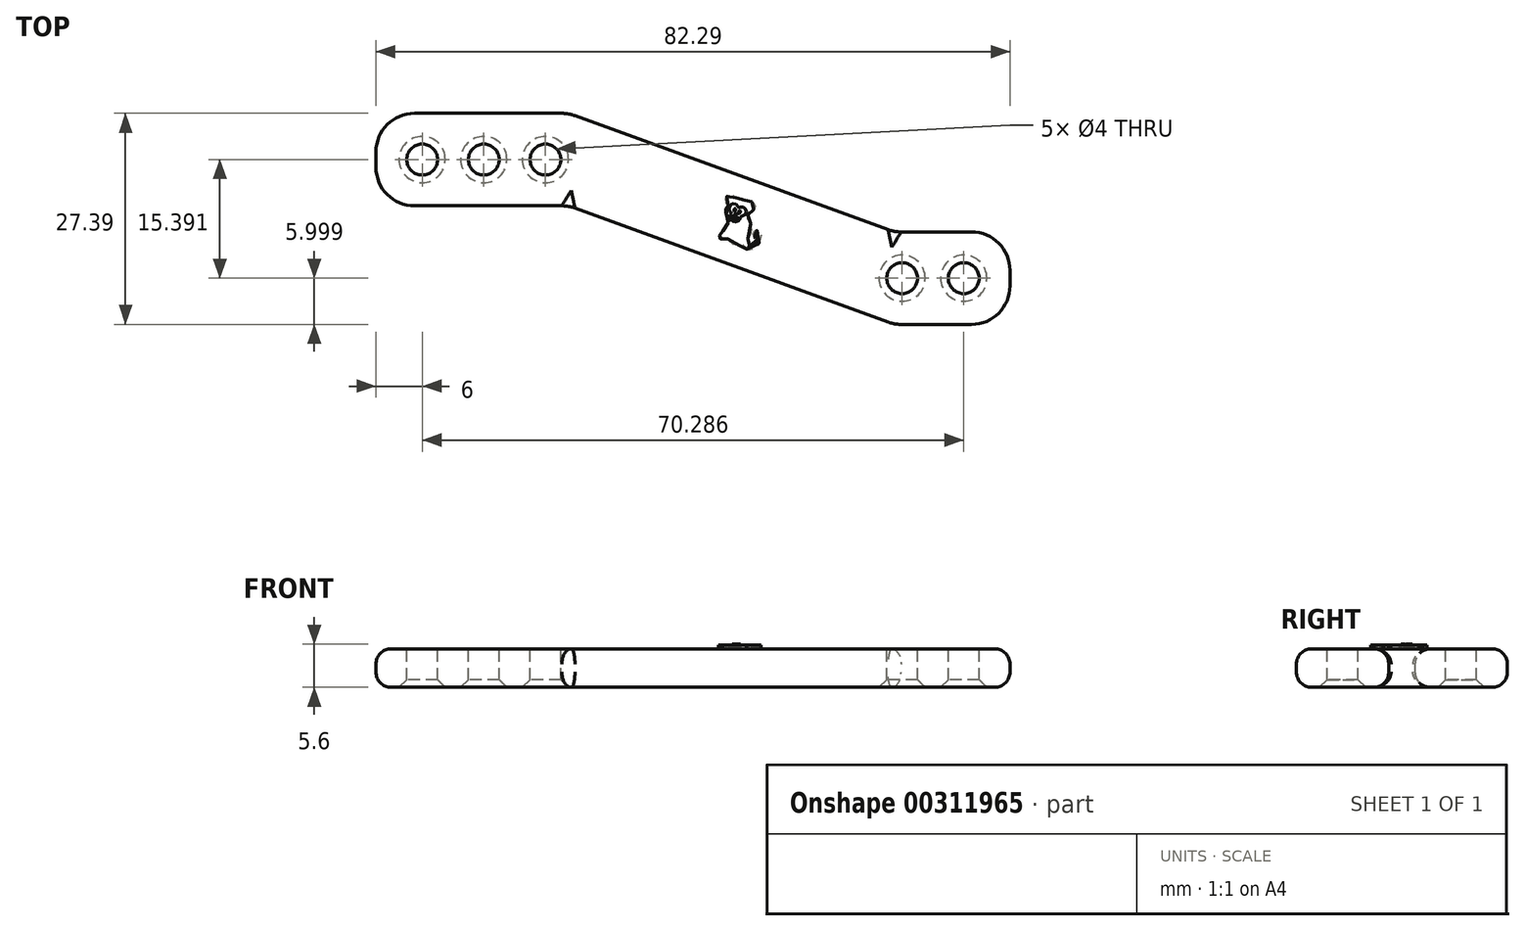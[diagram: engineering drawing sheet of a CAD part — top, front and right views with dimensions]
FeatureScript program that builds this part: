
annotation { "Feature Type Name" : "Feature", "Feature Type Description" : "" }
export const myFeature = defineFeature(function(context is Context, id is Id, definition is map)
    precondition{}
    {
        {
            var Q0;
            Q0=qCreatedBy(makeId("Top.planeOp"),FACE);
            var sketch = newSketch(context, id + "F0", { "sketchPlane" : qUnion([Q0])});
            skLineSegment(sketch, "E0.bottom", {"start": v(0, 12) * mm, "end": v(25, 12) * mm});
            skLineSegment(sketch, "E0.top", {"start": v(0, 0) * mm, "end": v(25, 0) * mm});
            skLineSegment(sketch, "E0.left", {"start": v(0, 12) * mm, "end": v(0, 0) * mm});
            skLineSegment(sketch, "E0.right", {"start": v(25, 12) * mm, "end": v(25, 0) * mm});
            skLineSegment(sketch, "E1.bottom", {"start": v(67.29, -3.4) * mm, "end": v(82.29, -3.4) * mm});
            skLineSegment(sketch, "E1.top", {"start": v(67.29, -15.4) * mm, "end": v(82.29, -15.4) * mm});
            skLineSegment(sketch, "E1.left", {"start": v(67.29, -3.4) * mm, "end": v(67.29, -15.4) * mm});
            skLineSegment(sketch, "E1.right", {"start": v(82.29, -3.4) * mm, "end": v(82.29, -15.4) * mm});
            skLineSegment(sketch, "E2", {"start": v(25, 12) * mm, "end": v(67.29, -3.4) * mm});
            skLineSegment(sketch, "E3", {"start": v(25, 0) * mm, "end": v(67.29, -15.4) * mm});
            skSolve(sketch);
        }
        {
            var Q0;
            Q0=makeQuery(id+"F0.imprint","IMPRINT",FACE,{"disambiguationData":[TD([[makeQuery(id+"F0.imprint","IMPRINT",EDGE,{"derivedFrom":sQuery(id+"F0.wireOp",EDGE,"E1.bottom")}),-1.0]])]});
            var Q1;
            Q1=makeQuery(id+"F0.imprint","IMPRINT",FACE,{"disambiguationData":[TD([[makeQuery(id+"F0.imprint","IMPRINT",EDGE,{"derivedFrom":sQuery(id+"F0.wireOp",EDGE,"E0.right")}),1.0]])]});
            var Q2;
            Q2=makeQuery(id+"F0.imprint","IMPRINT",FACE,{"disambiguationData":[TD([[makeQuery(id+"F0.imprint","IMPRINT",EDGE,{"derivedFrom":sQuery(id+"F0.wireOp",EDGE,"E0.bottom")}),-1.0]])]});
            extrude(context, id + "F1", {"entities" : qUnion([Q0, Q1, Q2]), "depth" : 5 * mm});
        }
        {
            var Q0;
            Q0=makeQuery(id+"F1.opExtrude","CAP_FACE",FACE,{"disambiguationData":[OSD([sQuery(id+"F0.wireOp",EDGE,"E0.bottom"),sQuery(id+"F0.wireOp",EDGE,"E0.top"),sQuery(id+"F0.wireOp",EDGE,"E0.left"),sQuery(id+"F0.wireOp",EDGE,"E1.bottom"),sQuery(id+"F0.wireOp",EDGE,"E1.top"),sQuery(id+"F0.wireOp",EDGE,"E1.right"),sQuery(id+"F0.wireOp",EDGE,"E2"),sQuery(id+"F0.wireOp",EDGE,"E3")])],"isStart":false});
            var sketch = newSketch(context, id + "F2", { "sketchPlane" : qUnion([Q0])});
            skCircle(sketch, "E4", {"center": v(6, 6) * mm, "radius": 2 * mm});
            skCircle(sketch, "E5", {"center": v(76.29, -9.4) * mm, "radius": 2 * mm});
            skCircle(sketch, "E6.1.0.0", {"center": v(14, 6) * mm, "radius": 2 * mm});
            skCircle(sketch, "E6.2.0.0", {"center": v(22, 6) * mm, "radius": 2 * mm});
            skLineSegment(sketch, "E6.direction1", {"start": v(6, 6) * mm, "end": v(14, 6) * mm, "construction": true});
            skCircle(sketch, "E7.1.0.0", {"center": v(68.29, -9.4) * mm, "radius": 2 * mm});
            skLineSegment(sketch, "E7.direction1", {"start": v(76.29, -9.4) * mm, "end": v(68.29, -9.4) * mm, "construction": true});
            skSolve(sketch);
        }
        {
            var Q0;
            Q0 = qSketchRegion(id + "F2", true);
            extrude(context, id + "F3", {"entities" : qUnion([Q0]), "operationType" : NewBodyOperationType.REMOVE, "endBound" : BoundingType.THROUGH_ALL, "oppositeDirection" : true, "depth" : 5 * mm});
        }
        {
            var Q0;
            Q0=makeQuery(id+"F1.opExtrude","CAP_EDGE",EDGE,{"disambiguationData":[OSD([sQuery(id+"F0.wireOp",EDGE,"E0.top")])],"isStart":false});
            var Q1;
            Q1=makeQuery(id+"F1.opExtrude","CAP_EDGE",EDGE,{"disambiguationData":[OSD([sQuery(id+"F0.wireOp",EDGE,"E3")])],"isStart":false});
            var Q2;
            Q2=makeQuery(id+"F1.opExtrude","CAP_EDGE",EDGE,{"disambiguationData":[OSD([sQuery(id+"F0.wireOp",EDGE,"E1.top")])],"isStart":false});
            var Q3;
            Q3=makeQuery(id+"F1.opExtrude","CAP_EDGE",EDGE,{"disambiguationData":[OSD([sQuery(id+"F0.wireOp",EDGE,"E1.right")])],"isStart":false});
            var Q4;
            Q4=makeQuery(id+"F1.opExtrude","CAP_EDGE",EDGE,{"disambiguationData":[OSD([sQuery(id+"F0.wireOp",EDGE,"E1.bottom")])],"isStart":false});
            var Q5;
            Q5=makeQuery(id+"F1.opExtrude","CAP_EDGE",EDGE,{"disambiguationData":[OSD([sQuery(id+"F0.wireOp",EDGE,"E2")])],"isStart":false});
            var Q6;
            Q6=makeQuery(id+"F1.opExtrude","CAP_EDGE",EDGE,{"disambiguationData":[OSD([sQuery(id+"F0.wireOp",EDGE,"E0.bottom")])],"isStart":false});
            var Q7;
            Q7=makeQuery(id+"F1.opExtrude","CAP_EDGE",EDGE,{"disambiguationData":[OSD([sQuery(id+"F0.wireOp",EDGE,"E0.left")])],"isStart":false});
            var Q8;
            Q8=makeQuery(id+"F1.opExtrude","CAP_EDGE",EDGE,{"disambiguationData":[OSD([sQuery(id+"F0.wireOp",EDGE,"E0.bottom")])],"isStart":true});
            var Q9;
            Q9=makeQuery(id+"F1.opExtrude","CAP_EDGE",EDGE,{"disambiguationData":[OSD([sQuery(id+"F0.wireOp",EDGE,"E2")])],"isStart":true});
            var Q10;
            Q10=makeQuery(id+"F1.opExtrude","CAP_EDGE",EDGE,{"disambiguationData":[OSD([sQuery(id+"F0.wireOp",EDGE,"E1.bottom")])],"isStart":true});
            var Q11;
            Q11=makeQuery(id+"F1.opExtrude","CAP_EDGE",EDGE,{"disambiguationData":[OSD([sQuery(id+"F0.wireOp",EDGE,"E1.right")])],"isStart":true});
            var Q12;
            Q12=makeQuery(id+"F1.opExtrude","CAP_EDGE",EDGE,{"disambiguationData":[OSD([sQuery(id+"F0.wireOp",EDGE,"E3")])],"isStart":true});
            var Q13;
            Q13=makeQuery(id+"F1.opExtrude","CAP_EDGE",EDGE,{"disambiguationData":[OSD([sQuery(id+"F0.wireOp",EDGE,"E0.left")])],"isStart":true});
            var Q14;
            Q14=makeQuery(id+"F1.opExtrude","CAP_EDGE",EDGE,{"disambiguationData":[OSD([sQuery(id+"F0.wireOp",EDGE,"E0.top")])],"isStart":true});
            var Q15;
            Q15=makeQuery(id+"F1.opExtrude","CAP_EDGE",EDGE,{"disambiguationData":[OSD([sQuery(id+"F0.wireOp",EDGE,"E1.top")])],"isStart":true});
            fillet(context, id + "F4", {"entities" : qUnion([Q0, Q1, Q2, Q3, Q4, Q5, Q6, Q7, Q8, Q9, Q10, Q11, Q12, Q13, Q14, Q15]), "radius" : 2 * mm, "tangentPropagation" : true, "allowEdgeOverflow" : false});
        }
        {
            var Q0;
            Q0=makeQuery(id+"F1.opExtrude","SWEPT_EDGE",EDGE,{"disambiguationData":[OSD([sQuery(id+"F0.wireOp",EDGE,"E0.bottom"),sQuery(id+"F0.wireOp",EDGE,"E0.left")])]});
            var Q1;
            Q1=makeQuery(id+"F1.opExtrude","SWEPT_EDGE",EDGE,{"disambiguationData":[OSD([sQuery(id+"F0.wireOp",EDGE,"E0.top"),sQuery(id+"F0.wireOp",EDGE,"E0.left")])]});
            var Q2;
            Q2=makeQuery(id+"F1.opExtrude","SWEPT_EDGE",EDGE,{"disambiguationData":[OSD([sQuery(id+"F0.wireOp",EDGE,"E1.bottom"),sQuery(id+"F0.wireOp",EDGE,"E1.right")])]});
            var Q3;
            Q3=makeQuery(id+"F1.opExtrude","SWEPT_EDGE",EDGE,{"disambiguationData":[OSD([sQuery(id+"F0.wireOp",EDGE,"E1.top"),sQuery(id+"F0.wireOp",EDGE,"E1.right")])]});
            var Q4;
            Q4=makeQuery(id+"F4.opFillet","BLEND_EDGE",EDGE,{"blendedFrom":[makeQuery(id+"F1.opExtrude","CAP_EDGE",EDGE,{"disambiguationData":[OSD([sQuery(id+"F0.wireOp",EDGE,"E1.top")])],"isStart":false}),makeQuery(id+"F1.opExtrude","CAP_EDGE",EDGE,{"disambiguationData":[OSD([sQuery(id+"F0.wireOp",EDGE,"E3")])],"isStart":false})],"blendedInto":[]});
            var Q5;
            Q5=makeQuery(id+"F4.opFillet","BLEND_EDGE",EDGE,{"blendedFrom":[makeQuery(id+"F1.opExtrude","CAP_EDGE",EDGE,{"disambiguationData":[OSD([sQuery(id+"F0.wireOp",EDGE,"E1.bottom")])],"isStart":false}),makeQuery(id+"F1.opExtrude","CAP_EDGE",EDGE,{"disambiguationData":[OSD([sQuery(id+"F0.wireOp",EDGE,"E2")])],"isStart":false})],"blendedInto":[]});
            var Q6;
            Q6=makeQuery(id+"F4.opFillet","BLEND_EDGE",EDGE,{"blendedFrom":[makeQuery(id+"F1.opExtrude","CAP_EDGE",EDGE,{"disambiguationData":[OSD([sQuery(id+"F0.wireOp",EDGE,"E0.top")])],"isStart":false}),makeQuery(id+"F1.opExtrude","CAP_EDGE",EDGE,{"disambiguationData":[OSD([sQuery(id+"F0.wireOp",EDGE,"E3")])],"isStart":false})],"blendedInto":[]});
            var Q7;
            Q7=makeQuery(id+"F4.opFillet","BLEND_EDGE",EDGE,{"blendedFrom":[makeQuery(id+"F1.opExtrude","CAP_EDGE",EDGE,{"disambiguationData":[OSD([sQuery(id+"F0.wireOp",EDGE,"E0.bottom")])],"isStart":false}),makeQuery(id+"F1.opExtrude","CAP_EDGE",EDGE,{"disambiguationData":[OSD([sQuery(id+"F0.wireOp",EDGE,"E2")])],"isStart":false})],"blendedInto":[]});
            var Q8;
            Q8=makeQuery(id+"F4.opFillet","BLEND_EDGE",EDGE,{"blendedFrom":[makeQuery(id+"F1.opExtrude","CAP_EDGE",EDGE,{"disambiguationData":[OSD([sQuery(id+"F0.wireOp",EDGE,"E0.top")])],"isStart":true}),makeQuery(id+"F1.opExtrude","CAP_EDGE",EDGE,{"disambiguationData":[OSD([sQuery(id+"F0.wireOp",EDGE,"E3")])],"isStart":true})],"blendedInto":[]});
            fillet(context, id + "F5", {"entities" : qUnion([Q0, Q1, Q2, Q3, Q4, Q5, Q6, Q7, Q8]), "radius" : 5 * mm, "tangentPropagation" : true, "allowEdgeOverflow" : false});
        }
        {
            var Q0;
            Q0=makeQuery(id+"F3.boolean.opBoolean","COPY",EDGE,{"derivedFrom":makeQuery(id+"F3.opExtrude","CAP_EDGE",EDGE,{"disambiguationData":[OSD([sQuery(id+"F2.wireOp",EDGE,"E6.2.0.0")])],"isStart":true})});
            var Q1;
            Q1=makeQuery(id+"F3.boolean.opBoolean","COPY",EDGE,{"derivedFrom":makeQuery(id+"F3.opExtrude","CAP_EDGE",EDGE,{"disambiguationData":[OSD([sQuery(id+"F2.wireOp",EDGE,"E6.1.0.0")])],"isStart":true})});
            var Q2;
            Q2=makeQuery(id+"F3.boolean.opBoolean","COPY",EDGE,{"derivedFrom":makeQuery(id+"F3.opExtrude","CAP_EDGE",EDGE,{"disambiguationData":[OSD([sQuery(id+"F2.wireOp",EDGE,"E4")])],"isStart":true})});
            var Q3;
            Q3=makeQuery(id+"F3.boolean.opBoolean","COPY",EDGE,{"derivedFrom":makeQuery(id+"F3.opExtrude","CAP_EDGE",EDGE,{"disambiguationData":[OSD([sQuery(id+"F2.wireOp",EDGE,"E7.1.0.0")])],"isStart":true})});
            var Q4;
            Q4=makeQuery(id+"F3.boolean.opBoolean","COPY",EDGE,{"derivedFrom":makeQuery(id+"F3.opExtrude","CAP_EDGE",EDGE,{"disambiguationData":[OSD([sQuery(id+"F2.wireOp",EDGE,"E5")])],"isStart":true})});
            var Q5;
            Q5=makeQuery(id+"F3.boolean.opBoolean","INTERSECT",EDGE,{"derivedFrom":[makeQuery(id+"F1.opExtrude","CAP_FACE",FACE,{"disambiguationData":[OSD([sQuery(id+"F0.wireOp",EDGE,"E0.bottom"),sQuery(id+"F0.wireOp",EDGE,"E0.top"),sQuery(id+"F0.wireOp",EDGE,"E0.left"),sQuery(id+"F0.wireOp",EDGE,"E1.bottom"),sQuery(id+"F0.wireOp",EDGE,"E1.top"),sQuery(id+"F0.wireOp",EDGE,"E1.right"),sQuery(id+"F0.wireOp",EDGE,"E2"),sQuery(id+"F0.wireOp",EDGE,"E3")])],"isStart":true}),makeQuery(id+"F3.opExtrude","SWEPT_FACE",FACE,{"disambiguationData":[OSD([sQuery(id+"F2.wireOp",EDGE,"E4")])]})]});
            var Q6;
            Q6=makeQuery(id+"F3.boolean.opBoolean","INTERSECT",EDGE,{"derivedFrom":[makeQuery(id+"F1.opExtrude","CAP_FACE",FACE,{"disambiguationData":[OSD([sQuery(id+"F0.wireOp",EDGE,"E0.bottom"),sQuery(id+"F0.wireOp",EDGE,"E0.top"),sQuery(id+"F0.wireOp",EDGE,"E0.left"),sQuery(id+"F0.wireOp",EDGE,"E1.bottom"),sQuery(id+"F0.wireOp",EDGE,"E1.top"),sQuery(id+"F0.wireOp",EDGE,"E1.right"),sQuery(id+"F0.wireOp",EDGE,"E2"),sQuery(id+"F0.wireOp",EDGE,"E3")])],"isStart":true}),makeQuery(id+"F3.opExtrude","SWEPT_FACE",FACE,{"disambiguationData":[OSD([sQuery(id+"F2.wireOp",EDGE,"E6.1.0.0")])]})]});
            var Q7;
            Q7=makeQuery(id+"F3.boolean.opBoolean","INTERSECT",EDGE,{"derivedFrom":[makeQuery(id+"F1.opExtrude","CAP_FACE",FACE,{"disambiguationData":[OSD([sQuery(id+"F0.wireOp",EDGE,"E0.bottom"),sQuery(id+"F0.wireOp",EDGE,"E0.top"),sQuery(id+"F0.wireOp",EDGE,"E0.left"),sQuery(id+"F0.wireOp",EDGE,"E1.bottom"),sQuery(id+"F0.wireOp",EDGE,"E1.top"),sQuery(id+"F0.wireOp",EDGE,"E1.right"),sQuery(id+"F0.wireOp",EDGE,"E2"),sQuery(id+"F0.wireOp",EDGE,"E3")])],"isStart":true}),makeQuery(id+"F3.opExtrude","SWEPT_FACE",FACE,{"disambiguationData":[OSD([sQuery(id+"F2.wireOp",EDGE,"E6.2.0.0")])]})]});
            var Q8;
            Q8=makeQuery(id+"F3.boolean.opBoolean","INTERSECT",EDGE,{"derivedFrom":[makeQuery(id+"F1.opExtrude","CAP_FACE",FACE,{"disambiguationData":[OSD([sQuery(id+"F0.wireOp",EDGE,"E0.bottom"),sQuery(id+"F0.wireOp",EDGE,"E0.top"),sQuery(id+"F0.wireOp",EDGE,"E0.left"),sQuery(id+"F0.wireOp",EDGE,"E1.bottom"),sQuery(id+"F0.wireOp",EDGE,"E1.top"),sQuery(id+"F0.wireOp",EDGE,"E1.right"),sQuery(id+"F0.wireOp",EDGE,"E2"),sQuery(id+"F0.wireOp",EDGE,"E3")])],"isStart":true}),makeQuery(id+"F3.opExtrude","SWEPT_FACE",FACE,{"disambiguationData":[OSD([sQuery(id+"F2.wireOp",EDGE,"E7.1.0.0")])]})]});
            var Q9;
            Q9=makeQuery(id+"F3.boolean.opBoolean","INTERSECT",EDGE,{"derivedFrom":[makeQuery(id+"F1.opExtrude","CAP_FACE",FACE,{"disambiguationData":[OSD([sQuery(id+"F0.wireOp",EDGE,"E0.bottom"),sQuery(id+"F0.wireOp",EDGE,"E0.top"),sQuery(id+"F0.wireOp",EDGE,"E0.left"),sQuery(id+"F0.wireOp",EDGE,"E1.bottom"),sQuery(id+"F0.wireOp",EDGE,"E1.top"),sQuery(id+"F0.wireOp",EDGE,"E1.right"),sQuery(id+"F0.wireOp",EDGE,"E2"),sQuery(id+"F0.wireOp",EDGE,"E3")])],"isStart":true}),makeQuery(id+"F3.opExtrude","SWEPT_FACE",FACE,{"disambiguationData":[OSD([sQuery(id+"F2.wireOp",EDGE,"E5")])]})]});
            chamfer(context, id + "F6", {"entities" : qUnion([Q0, Q1, Q2, Q3, Q4, Q5, Q6, Q7, Q8, Q9]), "width" : 1 * mm, "tangentPropagation" : true});
        }
        {
            var Q0;
            Q0=makeQuery(id+"F1.opExtrude","CAP_FACE",FACE,{"disambiguationData":[OSD([sQuery(id+"F0.wireOp",EDGE,"E0.bottom"),sQuery(id+"F0.wireOp",EDGE,"E0.top"),sQuery(id+"F0.wireOp",EDGE,"E0.left"),sQuery(id+"F0.wireOp",EDGE,"E1.bottom"),sQuery(id+"F0.wireOp",EDGE,"E1.top"),sQuery(id+"F0.wireOp",EDGE,"E1.right"),sQuery(id+"F0.wireOp",EDGE,"E2"),sQuery(id+"F0.wireOp",EDGE,"E3")])],"isStart":false});
            var sketch = newSketch(context, id + "F7", { "sketchPlane" : qUnion([Q0])});
            skFitSpline(sketch, "E8", {"points": [v(45.7, 0) * mm, v(45.5, 0.36) * mm, v(45.43, 0.85) * mm, v(45.6, 1.36) * mm, v(46.22, 1.5) * mm, v(46.75, 1.05) * mm, v(46.88, 1.05) * mm, v(47.42, 1.03) * mm, v(47.87, 0.73) * mm, v(48.05, 0.53) * mm, v(48.14, 0.62) * mm, v(48.62, 0.56) * mm, v(48.92, 0.44) * mm, v(49.2, 0) * mm, v(49.1, -0.36) * mm, v(48.76, -0.72) * mm, v(48.3, -0.85) * mm, v(48.29, -1.09) * mm, v(48.1, -1.56) * mm, v(48.33, -1.77) * mm, v(48.69, -2.54) * mm, v(48.6, -3.6) * mm, v(48.07, -4.73) * mm, v(48.1, -4.93) * mm, v(48.3, -5.16) * mm, v(48.83, -5.29) * mm, v(49.3, -4.75) * mm, v(49.56, -4.1) * mm, v(49.52, -3.6) * mm, v(49.5, -3.5) * mm, v(49.27, -3.5) * mm, v(49.21, -3.86) * mm, v(49.21, -4.04) * mm, v(49.32, -4.06) * mm, v(49.21, -4.17) * mm, v(49, -3.79) * mm, v(49.09, -3.31) * mm, v(49.41, -3.17) * mm, v(49.88, -3.44) * mm, v(49.7, -4.95) * mm, v(48.69, -5.74) * mm, v(47.96, -5.5) * mm, v(47.62, -4.98) * mm, v(47.47, -5.1) * mm, v(46.95, -5.16) * mm, v(45.95, -4.7) * mm, v(45.52, -4.15) * mm, v(45.4, -4.51) * mm, v(44.7, -4.3) * mm, v(44.68, -4.13) * mm, v(45.05, -4.22) * mm, v(44.63, -3.88) * mm, v(44.45, -3.64) * mm, v(44.6, -3.51) * mm, v(44.86, -3.5) * mm, v(45.08, -3.02) * mm, v(45.32, -2.66) * mm, v(45.48, -2.5) * mm, v(45.93, -1.72) * mm, v(45.75, -1.45) * mm, v(45.48, -1.09) * mm, v(45.4, -0.6) * mm, v(45.48, -0.27) * mm, v(45.7, 0) * mm]});
            skFitSpline(sketch, "E9", {"points": [v(46.18, -0.35) * mm, v(46.27, -0.26) * mm, v(46.39, -0.19) * mm, v(46.53, -0.25) * mm, v(46.55, -0.48) * mm, v(46.48, -0.67) * mm, v(46.3, -0.74) * mm, v(46.18, -0.63) * mm, v(46.18, -0.35) * mm]});
            skFitSpline(sketch, "E10", {"points": [v(47.29, -0.76) * mm, v(47.37, -0.62) * mm, v(47.54, -0.6) * mm, v(47.65, -0.77) * mm, v(47.59, -1) * mm, v(47.44, -1.15) * mm, v(47.28, -1.1) * mm, v(47.21, -0.93) * mm, v(47.29, -0.76) * mm]});
            skFitSpline(sketch, "E11", {"points": [v(46.24, -1.21) * mm, v(46.27, -1.4) * mm, v(46.42, -1.57) * mm, v(46.65, -1.7) * mm, v(46.95, -1.6) * mm, v(47.05, -1.51) * mm, v(46.8, -1.42) * mm, v(46.24, -1.21) * mm]});
            skCircle(sketch, "E12", {"center": v(46.65, -0.98) * mm, "radius": 0.07 * mm});
            skCircle(sketch, "E13", {"center": v(46.9, -1.06) * mm, "radius": 0.07 * mm});
            skFitSpline(sketch, "E14", {"points": [v(46.03, -0.81) * mm, v(45.86, -0.52) * mm, v(45.9, 0) * mm, v(46.25, 0.26) * mm, v(46.78, 0.14) * mm, v(47.04, -0.22) * mm, v(47.18, -0.25) * mm, v(47.34, -0.18) * mm, v(47.76, -0.22) * mm, v(48.03, -0.57) * mm, v(47.98, -1.09) * mm, v(47.43, -1.38) * mm, v(47.31, -1.53) * mm, v(47.21, -1.82) * mm, v(46.78, -2.07) * mm, v(46.36, -1.98) * mm, v(46.06, -1.75) * mm, v(45.9, -1.42) * mm, v(46.04, -1.09) * mm, v(46.11, -0.94) * mm, v(46.03, -0.81) * mm]});
            skSolve(sketch);
        }
        {
            var Q0;
            Q0 = qSketchRegion(id + "F7", true);
            extrude(context, id + "F8", {"entities" : qUnion([Q0]), "operationType" : NewBodyOperationType.ADD, "depth" : 0.5 * mm});
        }
        {
            var Q0;
            Q0=makeQuery(id+"F8.boolean.opBoolean","SPLIT",FACE,{"disambiguationData":[TD([makeQuery(id+"F8.opExtrude","SWEPT_FACE",FACE,{"disambiguationData":[OSD([sQuery(id+"F7.wireOp",EDGE,"E14")])]})])],"derivedFrom":makeQuery(id+"F1.opExtrude","CAP_FACE",FACE,{"disambiguationData":[OSD([sQuery(id+"F0.wireOp",EDGE,"E0.bottom"),sQuery(id+"F0.wireOp",EDGE,"E0.top"),sQuery(id+"F0.wireOp",EDGE,"E0.left"),sQuery(id+"F0.wireOp",EDGE,"E1.bottom"),sQuery(id+"F0.wireOp",EDGE,"E1.top"),sQuery(id+"F0.wireOp",EDGE,"E1.right"),sQuery(id+"F0.wireOp",EDGE,"E2"),sQuery(id+"F0.wireOp",EDGE,"E3")])],"isStart":false})});
            var sketch = newSketch(context, id + "F9", { "sketchPlane" : qUnion([Q0])});
            skEllipse(sketch, "E15", {"center": v(46.57, -0.56) * mm, "majorRadius": 0.2 * mm, "minorRadius": 0.1 * mm, "majorAxis": v(0.31, 0.95)});
            skEllipse(sketch, "E16.1.0.0", {"center": v(47.18, -0.8) * mm, "majorRadius": 0.2 * mm, "minorRadius": 0.1 * mm, "majorAxis": v(0.31, 0.95)});
            skLineSegment(sketch, "E16.direction1", {"start": v(46.57, -0.56) * mm, "end": v(47.18, -0.8) * mm, "construction": true});
            skFitSpline(sketch, "E17", {"points": [v(46.28, -1.28) * mm, v(46.5, -1.4) * mm, v(46.68, -1.47) * mm, v(46.96, -1.5) * mm, v(46.8, -1.75) * mm, v(46.38, -1.68) * mm, v(46.28, -1.28) * mm]});
            skCircle(sketch, "E18", {"center": v(46.67, -1.06) * mm, "radius": 0.05 * mm});
            skCircle(sketch, "E19.1.0.0", {"center": v(46.8, -1.12) * mm, "radius": 0.05 * mm});
            skLineSegment(sketch, "E19.direction1", {"start": v(46.67, -1.06) * mm, "end": v(46.8, -1.12) * mm, "construction": true});
            skSolve(sketch);
        }
        {
            var Q0;
            Q0=makeQuery(id+"F9.imprint","IMPRINT",FACE,{"disambiguationData":[TD([[makeQuery(id+"F9.imprint","IMPRINT",EDGE,{"derivedFrom":sQuery(id+"F9.wireOp",EDGE,"E15")}),1.0]])]});
            var Q1;
            Q1=makeQuery(id+"F9.imprint","IMPRINT",FACE,{"disambiguationData":[TD([[makeQuery(id+"F9.imprint","IMPRINT",EDGE,{"derivedFrom":sQuery(id+"F9.wireOp",EDGE,"E16.1.0.0")}),1.0]])]});
            var Q2;
            Q2=makeQuery(id+"F9.imprint","IMPRINT",FACE,{"disambiguationData":[TD([[makeQuery(id+"F9.imprint","IMPRINT",EDGE,{"derivedFrom":sQuery(id+"F9.wireOp",EDGE,"E18")}),1.0]])]});
            var Q3;
            Q3=makeQuery(id+"F9.imprint","IMPRINT",FACE,{"disambiguationData":[TD([[makeQuery(id+"F9.imprint","IMPRINT",EDGE,{"derivedFrom":sQuery(id+"F9.wireOp",EDGE,"E17")}),-1.0]])]});
            var Q4;
            Q4=makeQuery(id+"F9.imprint","IMPRINT",FACE,{"disambiguationData":[TD([[makeQuery(id+"F9.imprint","IMPRINT",EDGE,{"derivedFrom":sQuery(id+"F9.wireOp",EDGE,"E19.1.0.0")}),1.0]])]});
            var Q5;
            Q5=sQuery(id+"F9.wireOp",EDGE,"E15");
            var Q6;
            Q6=sQuery(id+"F9.wireOp",EDGE,"E16.1.0.0");
            var Q7;
            Q7=sQuery(id+"F9.wireOp",EDGE,"E19.1.0.0");
            var Q8;
            Q8=sQuery(id+"F9.wireOp",EDGE,"E18");
            var Q9;
            Q9=sQuery(id+"F9.wireOp",EDGE,"E17");
            extrude(context, id + "F10", {"entities" : qUnion([Q0, Q1, Q2, Q3, Q4]), "operationType" : NewBodyOperationType.ADD, "surfaceEntities" : qUnion([Q5, Q6, Q7, Q8, Q9]), "depth" : 0.6 * mm});
        }
    });
